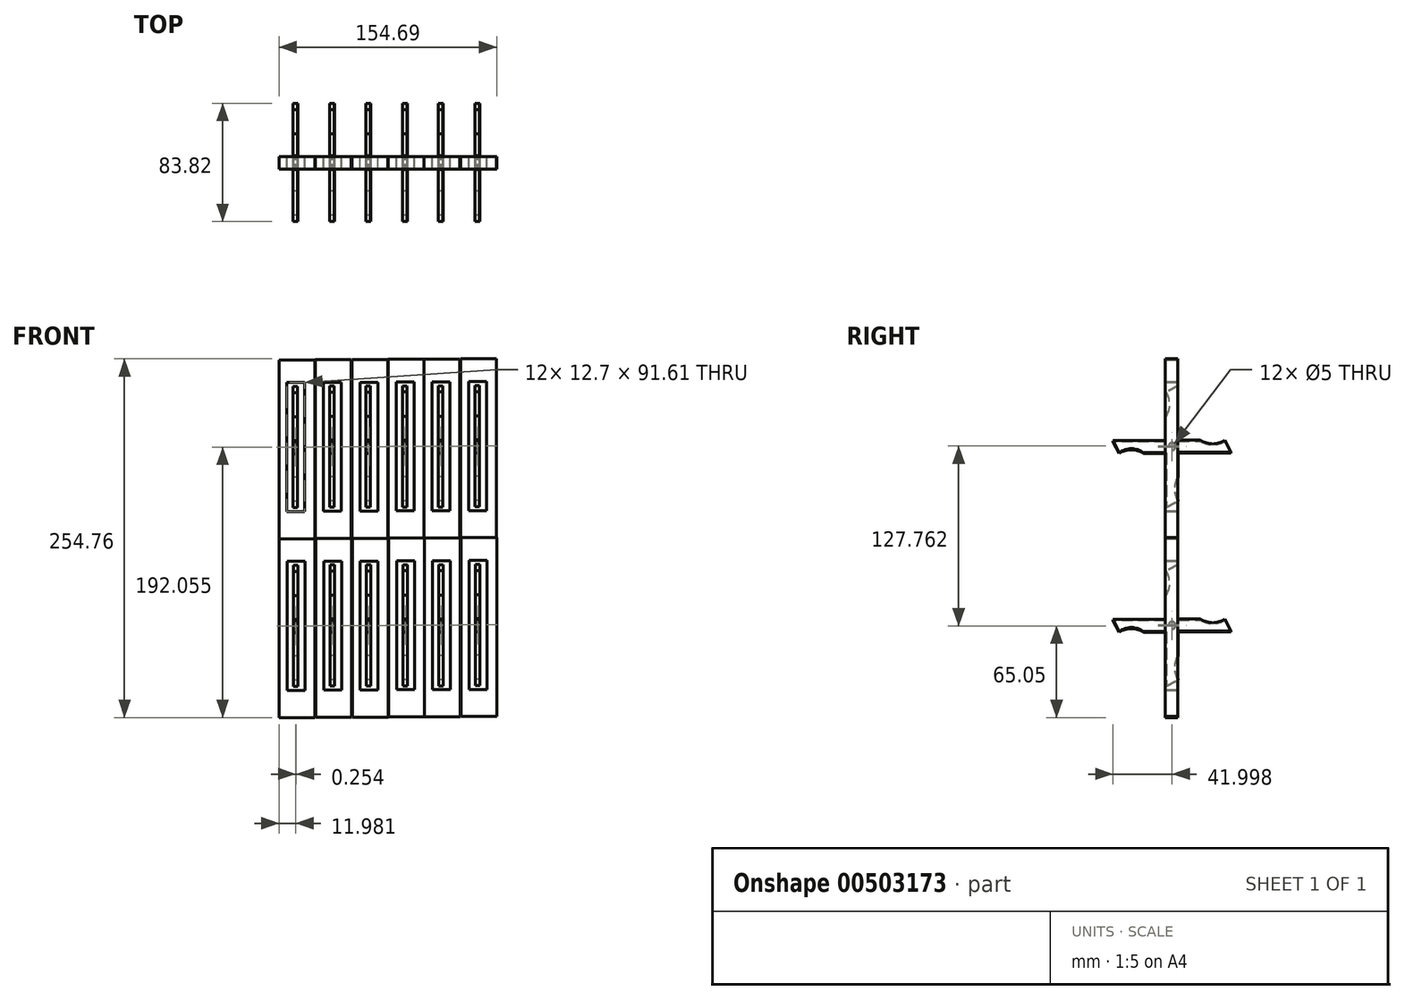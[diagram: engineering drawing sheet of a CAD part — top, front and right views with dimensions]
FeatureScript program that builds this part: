
annotation { "Feature Type Name" : "Feature", "Feature Type Description" : "" }
export const myFeature = defineFeature(function(context is Context, id is Id, definition is map)
    precondition{}
    {
        {
            var Q0;
            Q0=qCreatedBy(makeId("Front.planeOp"),FACE);
            var sketch = newSketch(context, id + "F0", { "sketchPlane" : qUnion([Q0])});
            skLineSegment(sketch, "E0", {"start": v(-10.05, 72.33) * mm, "end": v(15.35, 72.33) * mm});
            skLineSegment(sketch, "E1", {"start": v(-10.05, 72.33) * mm, "end": v(-10.05, -54.67) * mm});
            skLineSegment(sketch, "E2", {"start": v(8.28, 56.2) * mm, "end": v(8.28, -35.42) * mm});
            skLineSegment(sketch, "E3", {"start": v(-4.42, -35.42) * mm, "end": v(-4.42, 56.2) * mm});
            skLineSegment(sketch, "E4", {"start": v(15.35, 72.33) * mm, "end": v(15.35, -54.67) * mm});
            skLineSegment(sketch, "E5", {"start": v(-10.05, -54.67) * mm, "end": v(15.35, -54.67) * mm});
            skLineSegment(sketch, "E6", {"start": v(-4.42, 56.2) * mm, "end": v(8.28, 56.2) * mm});
            skLineSegment(sketch, "E7", {"start": v(-4.42, -35.42) * mm, "end": v(8.28, -35.42) * mm});
            skSolve(sketch);
        }
        {
            var Q0;
            Q0=qCreatedBy(makeId("Right.planeOp"),FACE);
            var sketch = newSketch(context, id + "F1", { "sketchPlane" : qUnion([Q0])});
            skCircle(sketch, "E8", {"center": v(-4.12, 10.38) * mm, "radius": 2.5 * mm});
            skCircle(sketch, "E9", {"center": v(-4.12, 10.38) * mm, "radius": 6.35 * mm});
            skLineSegment(sketch, "E10", {"start": v(-0.12, 15.3) * mm, "end": v(-0.12, 53.4) * mm});
            skLineSegment(sketch, "E11", {"start": v(-8.48, 15) * mm, "end": v(-8.48, 31.8) * mm});
            skArc(sketch, "E12", {"start": v(-8.48, 31.8) * mm, "mid": v(-5.82, 40.4) * mm, "end": v(-8.48, 49) * mm});
            skLineSegment(sketch, "E13", {"start": v(-0.12, 53.4) * mm, "end": v(-8.48, 49) * mm});
            skLineSegment(sketch, "E14.1.0", {"start": v(0.62, 6.16) * mm, "end": v(37.7, 6.16) * mm});
            skLineSegment(sketch, "E14.1.1", {"start": v(37.7, 6.16) * mm, "end": v(33.3, 14.53) * mm});
            skArc(sketch, "E14.1.2", {"start": v(16.1, 14.53) * mm, "mid": v(24.7, 11.87) * mm, "end": v(33.3, 14.53) * mm});
            skLineSegment(sketch, "E14.1.3", {"start": v(0.68, 14.53) * mm, "end": v(16.1, 14.53) * mm});
            skLineSegment(sketch, "E14.2.0", {"start": v(-9.23, 14.15) * mm, "end": v(-46.12, 14.15) * mm});
            skLineSegment(sketch, "E14.2.1", {"start": v(-46.12, 14.15) * mm, "end": v(-41.72, 5.79) * mm});
            skArc(sketch, "E14.2.2", {"start": v(-24.52, 5.79) * mm, "mid": v(-33.12, 8.44) * mm, "end": v(-41.72, 5.79) * mm});
            skLineSegment(sketch, "E14.2.3", {"start": v(-8.8, 5.79) * mm, "end": v(-24.52, 5.79) * mm});
            skPoint(sketch, "E14.center", {"position": v(-4.12, -16) * mm});
            skLineSegment(sketch, "E15", {"start": v(-8.8, 5.79) * mm, "end": v(-8.5, 5.79) * mm});
            skLineSegment(sketch, "E16.2.0", {"start": v(-8.13, 5.46) * mm, "end": v(-8.13, -32.64) * mm});
            skLineSegment(sketch, "E16.2.1", {"start": v(-8.13, -32.64) * mm, "end": v(0.24, -28.24) * mm});
            skArc(sketch, "E16.2.2", {"start": v(0.24, -11.04) * mm, "mid": v(-2.42, -19.64) * mm, "end": v(0.24, -28.24) * mm});
            skLineSegment(sketch, "E16.2.3", {"start": v(0.24, 5.77) * mm, "end": v(0.24, -11.04) * mm});
            skCircle(sketch, "E17", {"center": v(-4.12, 10.38) * mm, "radius": 1.87 * mm});
            skSolve(sketch);
        }
        {
            var Q0;
            Q0 = qSketchRegion(id + "F1", true);
            extrude(context, id + "F2", {"entities" : qUnion([Q0]), "depth" : 3.17 * mm});
        }
        {
            var Q0;
            Q0 = qSketchRegion(id + "F0", true);
            extrude(context, id + "F3", {"entities" : qUnion([Q0]), "operationType" : NewBodyOperationType.ADD, "depth" : 8.9 * mm});
        }
        {
            var Q0;
            Q0=sQuery(id+"F1.wireOp",EDGE,"E17");
            extrude(context, id + "F4", {"bodyType" : ToolBodyType.SURFACE, "surfaceEntities" : qUnion([Q0]), "endBound" : BoundingType.SYMMETRIC, "depth" : 16.5 * mm});
        }
        {
            var Q0;
            Q0=makeQuery(id+"F2.opExtrude","SWEPT_BODY",BODY,{"disambiguationData":[OSD([sQuery(id+"F1.wireOp",EDGE,"E8"),sQuery(id+"F1.wireOp",EDGE,"E9"),sQuery(id+"F1.wireOp",EDGE,"E10"),sQuery(id+"F1.wireOp",EDGE,"E11"),sQuery(id+"F1.wireOp",EDGE,"E12"),sQuery(id+"F1.wireOp",EDGE,"E13"),sQuery(id+"F1.wireOp",EDGE,"E14.1.0"),sQuery(id+"F1.wireOp",EDGE,"E14.1.1"),sQuery(id+"F1.wireOp",EDGE,"E14.1.2"),sQuery(id+"F1.wireOp",EDGE,"E14.1.3"),sQuery(id+"F1.wireOp",EDGE,"E14.2.0"),sQuery(id+"F1.wireOp",EDGE,"E14.2.1"),sQuery(id+"F1.wireOp",EDGE,"E14.2.2"),sQuery(id+"F1.wireOp",EDGE,"E14.2.3"),sQuery(id+"F1.wireOp",EDGE,"E15"),sQuery(id+"F1.wireOp",EDGE,"E16.2.0"),sQuery(id+"F1.wireOp",EDGE,"E16.2.1"),sQuery(id+"F1.wireOp",EDGE,"E16.2.2"),sQuery(id+"F1.wireOp",EDGE,"E16.2.3")])]});
            var Q1;
            Q1=makeQuery(id+"F4.opExtrude","SWEPT_BODY",BODY,{"disambiguationData":[OSD([sQuery(id+"F1.wireOp",EDGE,"E17")])]});
            var Q2;
            Q2=makeQuery(id+"F3.opExtrude","SWEPT_BODY",BODY,{"disambiguationData":[OSD([sQuery(id+"F0.wireOp",EDGE,"E0"),sQuery(id+"F0.wireOp",EDGE,"E1"),sQuery(id+"F0.wireOp",EDGE,"E2"),sQuery(id+"F0.wireOp",EDGE,"E3"),sQuery(id+"F0.wireOp",EDGE,"E4"),sQuery(id+"F0.wireOp",EDGE,"E5"),sQuery(id+"F0.wireOp",EDGE,"E6"),sQuery(id+"F0.wireOp",EDGE,"E7")])]});
            transform(context, id + "F5", {"entities" : qUnion([Q0, Q1, Q2]), "transformType" : TransformType.TRANSLATION_3D, "dx" : -65.28 * mm, "dy" : 0 * mm, "dz" : 3.3 * mm, "makeCopy" : false});
        }
        {
            var Q0;
            Q0=makeQuery(id+"F2.opExtrude","SWEPT_BODY",BODY,{"disambiguationData":[OSD([sQuery(id+"F1.wireOp",EDGE,"E8"),sQuery(id+"F1.wireOp",EDGE,"E9"),sQuery(id+"F1.wireOp",EDGE,"E10"),sQuery(id+"F1.wireOp",EDGE,"E11"),sQuery(id+"F1.wireOp",EDGE,"E12"),sQuery(id+"F1.wireOp",EDGE,"E13"),sQuery(id+"F1.wireOp",EDGE,"E14.1.0"),sQuery(id+"F1.wireOp",EDGE,"E14.1.1"),sQuery(id+"F1.wireOp",EDGE,"E14.1.2"),sQuery(id+"F1.wireOp",EDGE,"E14.1.3"),sQuery(id+"F1.wireOp",EDGE,"E14.2.0"),sQuery(id+"F1.wireOp",EDGE,"E14.2.1"),sQuery(id+"F1.wireOp",EDGE,"E14.2.2"),sQuery(id+"F1.wireOp",EDGE,"E14.2.3"),sQuery(id+"F1.wireOp",EDGE,"E15"),sQuery(id+"F1.wireOp",EDGE,"E16.2.0"),sQuery(id+"F1.wireOp",EDGE,"E16.2.1"),sQuery(id+"F1.wireOp",EDGE,"E16.2.2"),sQuery(id+"F1.wireOp",EDGE,"E16.2.3")])]});
            var Q1;
            Q1=makeQuery(id+"F4.opExtrude","SWEPT_BODY",BODY,{"disambiguationData":[OSD([sQuery(id+"F1.wireOp",EDGE,"E17")])]});
            var Q2;
            Q2=makeQuery(id+"F3.opExtrude","SWEPT_BODY",BODY,{"disambiguationData":[OSD([sQuery(id+"F0.wireOp",EDGE,"E0"),sQuery(id+"F0.wireOp",EDGE,"E1"),sQuery(id+"F0.wireOp",EDGE,"E2"),sQuery(id+"F0.wireOp",EDGE,"E3"),sQuery(id+"F0.wireOp",EDGE,"E4"),sQuery(id+"F0.wireOp",EDGE,"E5"),sQuery(id+"F0.wireOp",EDGE,"E6"),sQuery(id+"F0.wireOp",EDGE,"E7")])]});
            transform(context, id + "F6", {"entities" : qUnion([Q0, Q1, Q2]), "transformType" : TransformType.TRANSLATION_3D, "dx" : 25.9 * mm, "dy" : 0 * mm, "dz" : 0.25 * mm, "makeCopy" : true});
        }
        {
            var Q0;
            Q0=makeQuery(id+"F6.opPattern","COPY",BODY,{"derivedFrom":makeQuery(id+"F2.opExtrude","SWEPT_BODY",BODY,{"disambiguationData":[OSD([sQuery(id+"F1.wireOp",EDGE,"E8"),sQuery(id+"F1.wireOp",EDGE,"E9"),sQuery(id+"F1.wireOp",EDGE,"E10"),sQuery(id+"F1.wireOp",EDGE,"E11"),sQuery(id+"F1.wireOp",EDGE,"E12"),sQuery(id+"F1.wireOp",EDGE,"E13"),sQuery(id+"F1.wireOp",EDGE,"E14.1.0"),sQuery(id+"F1.wireOp",EDGE,"E14.1.1"),sQuery(id+"F1.wireOp",EDGE,"E14.1.2"),sQuery(id+"F1.wireOp",EDGE,"E14.1.3"),sQuery(id+"F1.wireOp",EDGE,"E14.2.0"),sQuery(id+"F1.wireOp",EDGE,"E14.2.1"),sQuery(id+"F1.wireOp",EDGE,"E14.2.2"),sQuery(id+"F1.wireOp",EDGE,"E14.2.3"),sQuery(id+"F1.wireOp",EDGE,"E15"),sQuery(id+"F1.wireOp",EDGE,"E16.2.0"),sQuery(id+"F1.wireOp",EDGE,"E16.2.1"),sQuery(id+"F1.wireOp",EDGE,"E16.2.2"),sQuery(id+"F1.wireOp",EDGE,"E16.2.3")])]}),"instanceName":"1"});
            var Q1;
            Q1=makeQuery(id+"F6.opPattern","COPY",BODY,{"derivedFrom":makeQuery(id+"F3.opExtrude","SWEPT_BODY",BODY,{"disambiguationData":[OSD([sQuery(id+"F0.wireOp",EDGE,"E0"),sQuery(id+"F0.wireOp",EDGE,"E1"),sQuery(id+"F0.wireOp",EDGE,"E2"),sQuery(id+"F0.wireOp",EDGE,"E3"),sQuery(id+"F0.wireOp",EDGE,"E4"),sQuery(id+"F0.wireOp",EDGE,"E5"),sQuery(id+"F0.wireOp",EDGE,"E6"),sQuery(id+"F0.wireOp",EDGE,"E7")])]}),"instanceName":"1"});
            var Q2;
            Q2=makeQuery(id+"F2.opExtrude","SWEPT_BODY",BODY,{"disambiguationData":[OSD([sQuery(id+"F1.wireOp",EDGE,"E8"),sQuery(id+"F1.wireOp",EDGE,"E9"),sQuery(id+"F1.wireOp",EDGE,"E10"),sQuery(id+"F1.wireOp",EDGE,"E11"),sQuery(id+"F1.wireOp",EDGE,"E12"),sQuery(id+"F1.wireOp",EDGE,"E13"),sQuery(id+"F1.wireOp",EDGE,"E14.1.0"),sQuery(id+"F1.wireOp",EDGE,"E14.1.1"),sQuery(id+"F1.wireOp",EDGE,"E14.1.2"),sQuery(id+"F1.wireOp",EDGE,"E14.1.3"),sQuery(id+"F1.wireOp",EDGE,"E14.2.0"),sQuery(id+"F1.wireOp",EDGE,"E14.2.1"),sQuery(id+"F1.wireOp",EDGE,"E14.2.2"),sQuery(id+"F1.wireOp",EDGE,"E14.2.3"),sQuery(id+"F1.wireOp",EDGE,"E15"),sQuery(id+"F1.wireOp",EDGE,"E16.2.0"),sQuery(id+"F1.wireOp",EDGE,"E16.2.1"),sQuery(id+"F1.wireOp",EDGE,"E16.2.2"),sQuery(id+"F1.wireOp",EDGE,"E16.2.3")])]});
            var Q3;
            Q3=makeQuery(id+"F4.opExtrude","SWEPT_BODY",BODY,{"disambiguationData":[OSD([sQuery(id+"F1.wireOp",EDGE,"E17")])]});
            var Q4;
            Q4=makeQuery(id+"F3.opExtrude","SWEPT_BODY",BODY,{"disambiguationData":[OSD([sQuery(id+"F0.wireOp",EDGE,"E0"),sQuery(id+"F0.wireOp",EDGE,"E1"),sQuery(id+"F0.wireOp",EDGE,"E2"),sQuery(id+"F0.wireOp",EDGE,"E3"),sQuery(id+"F0.wireOp",EDGE,"E4"),sQuery(id+"F0.wireOp",EDGE,"E5"),sQuery(id+"F0.wireOp",EDGE,"E6"),sQuery(id+"F0.wireOp",EDGE,"E7")])]});
            var Q5;
            Q5=makeQuery(id+"F6.opPattern","COPY",BODY,{"derivedFrom":makeQuery(id+"F4.opExtrude","SWEPT_BODY",BODY,{"disambiguationData":[OSD([sQuery(id+"F1.wireOp",EDGE,"E17")])]}),"instanceName":"1"});
            transform(context, id + "F7", {"entities" : qUnion([Q0, Q1, Q2, Q3, Q4, Q5]), "transformType" : TransformType.TRANSLATION_3D, "dx" : 51.82 * mm, "dy" : 0 * mm, "dz" : 0.25 * mm, "makeCopy" : true});
        }
        {
            var Q0;
            Q0=makeQuery(id+"F7.opPattern","COPY",BODY,{"derivedFrom":makeQuery(id+"F2.opExtrude","SWEPT_BODY",BODY,{"disambiguationData":[OSD([sQuery(id+"F1.wireOp",EDGE,"E8"),sQuery(id+"F1.wireOp",EDGE,"E9"),sQuery(id+"F1.wireOp",EDGE,"E10"),sQuery(id+"F1.wireOp",EDGE,"E11"),sQuery(id+"F1.wireOp",EDGE,"E12"),sQuery(id+"F1.wireOp",EDGE,"E13"),sQuery(id+"F1.wireOp",EDGE,"E14.1.0"),sQuery(id+"F1.wireOp",EDGE,"E14.1.1"),sQuery(id+"F1.wireOp",EDGE,"E14.1.2"),sQuery(id+"F1.wireOp",EDGE,"E14.1.3"),sQuery(id+"F1.wireOp",EDGE,"E14.2.0"),sQuery(id+"F1.wireOp",EDGE,"E14.2.1"),sQuery(id+"F1.wireOp",EDGE,"E14.2.2"),sQuery(id+"F1.wireOp",EDGE,"E14.2.3"),sQuery(id+"F1.wireOp",EDGE,"E15"),sQuery(id+"F1.wireOp",EDGE,"E16.2.0"),sQuery(id+"F1.wireOp",EDGE,"E16.2.1"),sQuery(id+"F1.wireOp",EDGE,"E16.2.2"),sQuery(id+"F1.wireOp",EDGE,"E16.2.3")])]}),"instanceName":"1"});
            var Q1;
            Q1=makeQuery(id+"F7.opPattern","COPY",BODY,{"derivedFrom":makeQuery(id+"F6.opPattern","COPY",BODY,{"derivedFrom":makeQuery(id+"F4.opExtrude","SWEPT_BODY",BODY,{"disambiguationData":[OSD([sQuery(id+"F1.wireOp",EDGE,"E17")])]}),"instanceName":"1"}),"instanceName":"1"});
            var Q2;
            Q2=makeQuery(id+"F7.opPattern","COPY",BODY,{"derivedFrom":makeQuery(id+"F4.opExtrude","SWEPT_BODY",BODY,{"disambiguationData":[OSD([sQuery(id+"F1.wireOp",EDGE,"E17")])]}),"instanceName":"1"});
            var Q3;
            Q3=makeQuery(id+"F7.opPattern","COPY",BODY,{"derivedFrom":makeQuery(id+"F6.opPattern","COPY",BODY,{"derivedFrom":makeQuery(id+"F2.opExtrude","SWEPT_BODY",BODY,{"disambiguationData":[OSD([sQuery(id+"F1.wireOp",EDGE,"E8"),sQuery(id+"F1.wireOp",EDGE,"E9"),sQuery(id+"F1.wireOp",EDGE,"E10"),sQuery(id+"F1.wireOp",EDGE,"E11"),sQuery(id+"F1.wireOp",EDGE,"E12"),sQuery(id+"F1.wireOp",EDGE,"E13"),sQuery(id+"F1.wireOp",EDGE,"E14.1.0"),sQuery(id+"F1.wireOp",EDGE,"E14.1.1"),sQuery(id+"F1.wireOp",EDGE,"E14.1.2"),sQuery(id+"F1.wireOp",EDGE,"E14.1.3"),sQuery(id+"F1.wireOp",EDGE,"E14.2.0"),sQuery(id+"F1.wireOp",EDGE,"E14.2.1"),sQuery(id+"F1.wireOp",EDGE,"E14.2.2"),sQuery(id+"F1.wireOp",EDGE,"E14.2.3"),sQuery(id+"F1.wireOp",EDGE,"E15"),sQuery(id+"F1.wireOp",EDGE,"E16.2.0"),sQuery(id+"F1.wireOp",EDGE,"E16.2.1"),sQuery(id+"F1.wireOp",EDGE,"E16.2.2"),sQuery(id+"F1.wireOp",EDGE,"E16.2.3")])]}),"instanceName":"1"}),"instanceName":"1"});
            var Q4;
            Q4=makeQuery(id+"F7.opPattern","COPY",BODY,{"derivedFrom":makeQuery(id+"F3.opExtrude","SWEPT_BODY",BODY,{"disambiguationData":[OSD([sQuery(id+"F0.wireOp",EDGE,"E0"),sQuery(id+"F0.wireOp",EDGE,"E1"),sQuery(id+"F0.wireOp",EDGE,"E2"),sQuery(id+"F0.wireOp",EDGE,"E3"),sQuery(id+"F0.wireOp",EDGE,"E4"),sQuery(id+"F0.wireOp",EDGE,"E5"),sQuery(id+"F0.wireOp",EDGE,"E6"),sQuery(id+"F0.wireOp",EDGE,"E7")])]}),"instanceName":"1"});
            var Q5;
            Q5=makeQuery(id+"F7.opPattern","COPY",BODY,{"derivedFrom":makeQuery(id+"F6.opPattern","COPY",BODY,{"derivedFrom":makeQuery(id+"F3.opExtrude","SWEPT_BODY",BODY,{"disambiguationData":[OSD([sQuery(id+"F0.wireOp",EDGE,"E0"),sQuery(id+"F0.wireOp",EDGE,"E1"),sQuery(id+"F0.wireOp",EDGE,"E2"),sQuery(id+"F0.wireOp",EDGE,"E3"),sQuery(id+"F0.wireOp",EDGE,"E4"),sQuery(id+"F0.wireOp",EDGE,"E5"),sQuery(id+"F0.wireOp",EDGE,"E6"),sQuery(id+"F0.wireOp",EDGE,"E7")])]}),"instanceName":"1"}),"instanceName":"1"});
            transform(context, id + "F8", {"entities" : qUnion([Q0, Q1, Q2, Q3, Q4, Q5]), "transformType" : TransformType.TRANSLATION_3D, "dx" : 51.3 * mm, "dy" : 0 * mm, "dz" : 0.25 * mm, "makeCopy" : true});
        }
        {
            var Q0;
            Q0=makeQuery(id+"F7.opPattern","COPY",BODY,{"derivedFrom":makeQuery(id+"F2.opExtrude","SWEPT_BODY",BODY,{"disambiguationData":[OSD([sQuery(id+"F1.wireOp",EDGE,"E8"),sQuery(id+"F1.wireOp",EDGE,"E9"),sQuery(id+"F1.wireOp",EDGE,"E10"),sQuery(id+"F1.wireOp",EDGE,"E11"),sQuery(id+"F1.wireOp",EDGE,"E12"),sQuery(id+"F1.wireOp",EDGE,"E13"),sQuery(id+"F1.wireOp",EDGE,"E14.1.0"),sQuery(id+"F1.wireOp",EDGE,"E14.1.1"),sQuery(id+"F1.wireOp",EDGE,"E14.1.2"),sQuery(id+"F1.wireOp",EDGE,"E14.1.3"),sQuery(id+"F1.wireOp",EDGE,"E14.2.0"),sQuery(id+"F1.wireOp",EDGE,"E14.2.1"),sQuery(id+"F1.wireOp",EDGE,"E14.2.2"),sQuery(id+"F1.wireOp",EDGE,"E14.2.3"),sQuery(id+"F1.wireOp",EDGE,"E15"),sQuery(id+"F1.wireOp",EDGE,"E16.2.0"),sQuery(id+"F1.wireOp",EDGE,"E16.2.1"),sQuery(id+"F1.wireOp",EDGE,"E16.2.2"),sQuery(id+"F1.wireOp",EDGE,"E16.2.3")])]}),"instanceName":"1"});
            var Q1;
            Q1=makeQuery(id+"F6.opPattern","COPY",BODY,{"derivedFrom":makeQuery(id+"F2.opExtrude","SWEPT_BODY",BODY,{"disambiguationData":[OSD([sQuery(id+"F1.wireOp",EDGE,"E8"),sQuery(id+"F1.wireOp",EDGE,"E9"),sQuery(id+"F1.wireOp",EDGE,"E10"),sQuery(id+"F1.wireOp",EDGE,"E11"),sQuery(id+"F1.wireOp",EDGE,"E12"),sQuery(id+"F1.wireOp",EDGE,"E13"),sQuery(id+"F1.wireOp",EDGE,"E14.1.0"),sQuery(id+"F1.wireOp",EDGE,"E14.1.1"),sQuery(id+"F1.wireOp",EDGE,"E14.1.2"),sQuery(id+"F1.wireOp",EDGE,"E14.1.3"),sQuery(id+"F1.wireOp",EDGE,"E14.2.0"),sQuery(id+"F1.wireOp",EDGE,"E14.2.1"),sQuery(id+"F1.wireOp",EDGE,"E14.2.2"),sQuery(id+"F1.wireOp",EDGE,"E14.2.3"),sQuery(id+"F1.wireOp",EDGE,"E15"),sQuery(id+"F1.wireOp",EDGE,"E16.2.0"),sQuery(id+"F1.wireOp",EDGE,"E16.2.1"),sQuery(id+"F1.wireOp",EDGE,"E16.2.2"),sQuery(id+"F1.wireOp",EDGE,"E16.2.3")])]}),"instanceName":"1"});
            var Q2;
            Q2=makeQuery(id+"F6.opPattern","COPY",BODY,{"derivedFrom":makeQuery(id+"F3.opExtrude","SWEPT_BODY",BODY,{"disambiguationData":[OSD([sQuery(id+"F0.wireOp",EDGE,"E0"),sQuery(id+"F0.wireOp",EDGE,"E1"),sQuery(id+"F0.wireOp",EDGE,"E2"),sQuery(id+"F0.wireOp",EDGE,"E3"),sQuery(id+"F0.wireOp",EDGE,"E4"),sQuery(id+"F0.wireOp",EDGE,"E5"),sQuery(id+"F0.wireOp",EDGE,"E6"),sQuery(id+"F0.wireOp",EDGE,"E7")])]}),"instanceName":"1"});
            var Q3;
            Q3=makeQuery(id+"F8.opPattern","COPY",BODY,{"derivedFrom":makeQuery(id+"F7.opPattern","COPY",BODY,{"derivedFrom":makeQuery(id+"F3.opExtrude","SWEPT_BODY",BODY,{"disambiguationData":[OSD([sQuery(id+"F0.wireOp",EDGE,"E0"),sQuery(id+"F0.wireOp",EDGE,"E1"),sQuery(id+"F0.wireOp",EDGE,"E2"),sQuery(id+"F0.wireOp",EDGE,"E3"),sQuery(id+"F0.wireOp",EDGE,"E4"),sQuery(id+"F0.wireOp",EDGE,"E5"),sQuery(id+"F0.wireOp",EDGE,"E6"),sQuery(id+"F0.wireOp",EDGE,"E7")])]}),"instanceName":"1"}),"instanceName":"1"});
            var Q4;
            Q4=makeQuery(id+"F8.opPattern","COPY",BODY,{"derivedFrom":makeQuery(id+"F7.opPattern","COPY",BODY,{"derivedFrom":makeQuery(id+"F6.opPattern","COPY",BODY,{"derivedFrom":makeQuery(id+"F3.opExtrude","SWEPT_BODY",BODY,{"disambiguationData":[OSD([sQuery(id+"F0.wireOp",EDGE,"E0"),sQuery(id+"F0.wireOp",EDGE,"E1"),sQuery(id+"F0.wireOp",EDGE,"E2"),sQuery(id+"F0.wireOp",EDGE,"E3"),sQuery(id+"F0.wireOp",EDGE,"E4"),sQuery(id+"F0.wireOp",EDGE,"E5"),sQuery(id+"F0.wireOp",EDGE,"E6"),sQuery(id+"F0.wireOp",EDGE,"E7")])]}),"instanceName":"1"}),"instanceName":"1"}),"instanceName":"1"});
            var Q5;
            Q5=makeQuery(id+"F8.opPattern","COPY",BODY,{"derivedFrom":makeQuery(id+"F7.opPattern","COPY",BODY,{"derivedFrom":makeQuery(id+"F6.opPattern","COPY",BODY,{"derivedFrom":makeQuery(id+"F2.opExtrude","SWEPT_BODY",BODY,{"disambiguationData":[OSD([sQuery(id+"F1.wireOp",EDGE,"E8"),sQuery(id+"F1.wireOp",EDGE,"E9"),sQuery(id+"F1.wireOp",EDGE,"E10"),sQuery(id+"F1.wireOp",EDGE,"E11"),sQuery(id+"F1.wireOp",EDGE,"E12"),sQuery(id+"F1.wireOp",EDGE,"E13"),sQuery(id+"F1.wireOp",EDGE,"E14.1.0"),sQuery(id+"F1.wireOp",EDGE,"E14.1.1"),sQuery(id+"F1.wireOp",EDGE,"E14.1.2"),sQuery(id+"F1.wireOp",EDGE,"E14.1.3"),sQuery(id+"F1.wireOp",EDGE,"E14.2.0"),sQuery(id+"F1.wireOp",EDGE,"E14.2.1"),sQuery(id+"F1.wireOp",EDGE,"E14.2.2"),sQuery(id+"F1.wireOp",EDGE,"E14.2.3"),sQuery(id+"F1.wireOp",EDGE,"E15"),sQuery(id+"F1.wireOp",EDGE,"E16.2.0"),sQuery(id+"F1.wireOp",EDGE,"E16.2.1"),sQuery(id+"F1.wireOp",EDGE,"E16.2.2"),sQuery(id+"F1.wireOp",EDGE,"E16.2.3")])]}),"instanceName":"1"}),"instanceName":"1"}),"instanceName":"1"});
            var Q6;
            Q6=makeQuery(id+"F2.opExtrude","SWEPT_BODY",BODY,{"disambiguationData":[OSD([sQuery(id+"F1.wireOp",EDGE,"E8"),sQuery(id+"F1.wireOp",EDGE,"E9"),sQuery(id+"F1.wireOp",EDGE,"E10"),sQuery(id+"F1.wireOp",EDGE,"E11"),sQuery(id+"F1.wireOp",EDGE,"E12"),sQuery(id+"F1.wireOp",EDGE,"E13"),sQuery(id+"F1.wireOp",EDGE,"E14.1.0"),sQuery(id+"F1.wireOp",EDGE,"E14.1.1"),sQuery(id+"F1.wireOp",EDGE,"E14.1.2"),sQuery(id+"F1.wireOp",EDGE,"E14.1.3"),sQuery(id+"F1.wireOp",EDGE,"E14.2.0"),sQuery(id+"F1.wireOp",EDGE,"E14.2.1"),sQuery(id+"F1.wireOp",EDGE,"E14.2.2"),sQuery(id+"F1.wireOp",EDGE,"E14.2.3"),sQuery(id+"F1.wireOp",EDGE,"E15"),sQuery(id+"F1.wireOp",EDGE,"E16.2.0"),sQuery(id+"F1.wireOp",EDGE,"E16.2.1"),sQuery(id+"F1.wireOp",EDGE,"E16.2.2"),sQuery(id+"F1.wireOp",EDGE,"E16.2.3")])]});
            var Q7;
            Q7=makeQuery(id+"F8.opPattern","COPY",BODY,{"derivedFrom":makeQuery(id+"F7.opPattern","COPY",BODY,{"derivedFrom":makeQuery(id+"F2.opExtrude","SWEPT_BODY",BODY,{"disambiguationData":[OSD([sQuery(id+"F1.wireOp",EDGE,"E8"),sQuery(id+"F1.wireOp",EDGE,"E9"),sQuery(id+"F1.wireOp",EDGE,"E10"),sQuery(id+"F1.wireOp",EDGE,"E11"),sQuery(id+"F1.wireOp",EDGE,"E12"),sQuery(id+"F1.wireOp",EDGE,"E13"),sQuery(id+"F1.wireOp",EDGE,"E14.1.0"),sQuery(id+"F1.wireOp",EDGE,"E14.1.1"),sQuery(id+"F1.wireOp",EDGE,"E14.1.2"),sQuery(id+"F1.wireOp",EDGE,"E14.1.3"),sQuery(id+"F1.wireOp",EDGE,"E14.2.0"),sQuery(id+"F1.wireOp",EDGE,"E14.2.1"),sQuery(id+"F1.wireOp",EDGE,"E14.2.2"),sQuery(id+"F1.wireOp",EDGE,"E14.2.3"),sQuery(id+"F1.wireOp",EDGE,"E15"),sQuery(id+"F1.wireOp",EDGE,"E16.2.0"),sQuery(id+"F1.wireOp",EDGE,"E16.2.1"),sQuery(id+"F1.wireOp",EDGE,"E16.2.2"),sQuery(id+"F1.wireOp",EDGE,"E16.2.3")])]}),"instanceName":"1"}),"instanceName":"1"});
            var Q8;
            Q8=makeQuery(id+"F7.opPattern","COPY",BODY,{"derivedFrom":makeQuery(id+"F6.opPattern","COPY",BODY,{"derivedFrom":makeQuery(id+"F2.opExtrude","SWEPT_BODY",BODY,{"disambiguationData":[OSD([sQuery(id+"F1.wireOp",EDGE,"E8"),sQuery(id+"F1.wireOp",EDGE,"E9"),sQuery(id+"F1.wireOp",EDGE,"E10"),sQuery(id+"F1.wireOp",EDGE,"E11"),sQuery(id+"F1.wireOp",EDGE,"E12"),sQuery(id+"F1.wireOp",EDGE,"E13"),sQuery(id+"F1.wireOp",EDGE,"E14.1.0"),sQuery(id+"F1.wireOp",EDGE,"E14.1.1"),sQuery(id+"F1.wireOp",EDGE,"E14.1.2"),sQuery(id+"F1.wireOp",EDGE,"E14.1.3"),sQuery(id+"F1.wireOp",EDGE,"E14.2.0"),sQuery(id+"F1.wireOp",EDGE,"E14.2.1"),sQuery(id+"F1.wireOp",EDGE,"E14.2.2"),sQuery(id+"F1.wireOp",EDGE,"E14.2.3"),sQuery(id+"F1.wireOp",EDGE,"E15"),sQuery(id+"F1.wireOp",EDGE,"E16.2.0"),sQuery(id+"F1.wireOp",EDGE,"E16.2.1"),sQuery(id+"F1.wireOp",EDGE,"E16.2.2"),sQuery(id+"F1.wireOp",EDGE,"E16.2.3")])]}),"instanceName":"1"}),"instanceName":"1"});
            var Q9;
            Q9=makeQuery(id+"F3.opExtrude","SWEPT_BODY",BODY,{"disambiguationData":[OSD([sQuery(id+"F0.wireOp",EDGE,"E0"),sQuery(id+"F0.wireOp",EDGE,"E1"),sQuery(id+"F0.wireOp",EDGE,"E2"),sQuery(id+"F0.wireOp",EDGE,"E3"),sQuery(id+"F0.wireOp",EDGE,"E4"),sQuery(id+"F0.wireOp",EDGE,"E5"),sQuery(id+"F0.wireOp",EDGE,"E6"),sQuery(id+"F0.wireOp",EDGE,"E7")])]});
            var Q10;
            Q10=makeQuery(id+"F7.opPattern","COPY",BODY,{"derivedFrom":makeQuery(id+"F3.opExtrude","SWEPT_BODY",BODY,{"disambiguationData":[OSD([sQuery(id+"F0.wireOp",EDGE,"E0"),sQuery(id+"F0.wireOp",EDGE,"E1"),sQuery(id+"F0.wireOp",EDGE,"E2"),sQuery(id+"F0.wireOp",EDGE,"E3"),sQuery(id+"F0.wireOp",EDGE,"E4"),sQuery(id+"F0.wireOp",EDGE,"E5"),sQuery(id+"F0.wireOp",EDGE,"E6"),sQuery(id+"F0.wireOp",EDGE,"E7")])]}),"instanceName":"1"});
            var Q11;
            Q11=makeQuery(id+"F7.opPattern","COPY",BODY,{"derivedFrom":makeQuery(id+"F6.opPattern","COPY",BODY,{"derivedFrom":makeQuery(id+"F3.opExtrude","SWEPT_BODY",BODY,{"disambiguationData":[OSD([sQuery(id+"F0.wireOp",EDGE,"E0"),sQuery(id+"F0.wireOp",EDGE,"E1"),sQuery(id+"F0.wireOp",EDGE,"E2"),sQuery(id+"F0.wireOp",EDGE,"E3"),sQuery(id+"F0.wireOp",EDGE,"E4"),sQuery(id+"F0.wireOp",EDGE,"E5"),sQuery(id+"F0.wireOp",EDGE,"E6"),sQuery(id+"F0.wireOp",EDGE,"E7")])]}),"instanceName":"1"}),"instanceName":"1"});
            var Q12;
            Q12=makeQuery(id+"F8.opPattern","COPY",BODY,{"derivedFrom":makeQuery(id+"F7.opPattern","COPY",BODY,{"derivedFrom":makeQuery(id+"F6.opPattern","COPY",BODY,{"derivedFrom":makeQuery(id+"F4.opExtrude","SWEPT_BODY",BODY,{"disambiguationData":[OSD([sQuery(id+"F1.wireOp",EDGE,"E17")])]}),"instanceName":"1"}),"instanceName":"1"}),"instanceName":"1"});
            var Q13;
            Q13=makeQuery(id+"F7.opPattern","COPY",BODY,{"derivedFrom":makeQuery(id+"F6.opPattern","COPY",BODY,{"derivedFrom":makeQuery(id+"F4.opExtrude","SWEPT_BODY",BODY,{"disambiguationData":[OSD([sQuery(id+"F1.wireOp",EDGE,"E17")])]}),"instanceName":"1"}),"instanceName":"1"});
            var Q14;
            Q14=makeQuery(id+"F4.opExtrude","SWEPT_BODY",BODY,{"disambiguationData":[OSD([sQuery(id+"F1.wireOp",EDGE,"E17")])]});
            var Q15;
            Q15=makeQuery(id+"F8.opPattern","COPY",BODY,{"derivedFrom":makeQuery(id+"F7.opPattern","COPY",BODY,{"derivedFrom":makeQuery(id+"F4.opExtrude","SWEPT_BODY",BODY,{"disambiguationData":[OSD([sQuery(id+"F1.wireOp",EDGE,"E17")])]}),"instanceName":"1"}),"instanceName":"1"});
            var Q16;
            Q16=makeQuery(id+"F7.opPattern","COPY",BODY,{"derivedFrom":makeQuery(id+"F4.opExtrude","SWEPT_BODY",BODY,{"disambiguationData":[OSD([sQuery(id+"F1.wireOp",EDGE,"E17")])]}),"instanceName":"1"});
            var Q17;
            Q17=makeQuery(id+"F6.opPattern","COPY",BODY,{"derivedFrom":makeQuery(id+"F4.opExtrude","SWEPT_BODY",BODY,{"disambiguationData":[OSD([sQuery(id+"F1.wireOp",EDGE,"E17")])]}),"instanceName":"1"});
            transform(context, id + "F9", {"entities" : qUnion([Q0, Q1, Q2, Q3, Q4, Q5, Q6, Q7, Q8, Q9, Q10, Q11, Q12, Q13, Q14, Q15, Q16, Q17]), "transformType" : TransformType.TRANSLATION_3D, "dx" : 0.25 * mm, "dy" : 0 * mm, "dz" : -127 * mm, "makeCopy" : true});
        }
    });
